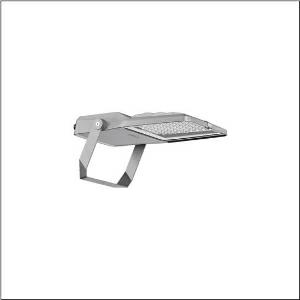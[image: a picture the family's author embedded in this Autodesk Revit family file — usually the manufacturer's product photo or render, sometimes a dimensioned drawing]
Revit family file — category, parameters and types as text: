
# Revit family: floodlight_fl_21_iq_mini___pl52_5xa7772c3d1a_c98d
name_source: partatom
category: Lighting Fixtures
units: mm (PartAtom-declared; Revit-internal decimal feet)

## family parameters
Cut with Voids When Loaded = No
Host = Face
Light Source = No
Part Type = Normal
Room Calculation Point = No
Round Connector Dimension = Use Diameter
Shared = No

## types (1)
- --- (1 x LED, 10510 lm, 87.2 W, 3000K)
    Apparent Load = 87 VA
    CIE Flux Codes = 26 60 98 100 100
    Color Rendering = 80
    Color Temperature = 3000K
    Default Elevation = 1800 mm
    Description = Floodlight FL 21 iQ mini, floodlight, primary light control with lens, of PMMA, primary optical cover: protective disc, of toughened safety glass, transparent, light distribution: PL52, light emission: direct distribution, installation type: surface-mounted, LED, High Power LED, rated luminous flux: 10.510lm, luminous efficacy: 121lm/W, light colour: 830, colour temperature: 3000K, control gear: iQ Street-Remote/DALI, control: Street-Remote, Auto-Match, Temp-Guard, Night-Set, Smart-Wire, Desk-Remote (wireless, voltage-free reading and setting of iQ features in the workshop via application-optimized NFC function/RFID function), optimised constant luminous flux control (CLO 2.0), with terminal, 6-pole, mains connection: 220..240V, AC, 50/60Hz, start of lifetime: 87W, end of service life: 92W, reduction: 40W, luminaire housing, of diecast aluminium, powder-coated, Siteco® metallic grey (DB 702S), corrosivity category C5 mid according to DIN EN ISO 12944, suitable for swimming pools, chlorine-resistant, sealing non-destructively replaceable, mounting bracket, of steel, galvanised, powder-coated, Siteco® metallic grey (DB 702S), protection rating (complete): IP66, insulation class (complete): insulation class II (safety insulation), certification: CE, ENEC, VDE, protection symbol: D, impact resistance: IK08, permissible operating ambient temperature: -40..+40°C, permissible operating ambient temperature for outdoor applications: -40..+50°C, standard: DIN EN 12944, LABS conformity tested according to VDMA 24364:2018-05, packaging unit: 1 piece

Light Distribution: PL52
    Height = 70 mm
    Lamp = 1 x LED
    Lamp Light Flux = 10510 lm
    Lamp Power = 87.2 W
    Lamp count = 1
    Length = 485 mm
    Luminous efficacy = 121 lm/W
    Manufacturer = Siteco
    ModVariant = No
    Model = 5XA7772C3D1A
    Number of Poles = 1
    OnlyDefault = Yes
    Power Factor = 1
    Product Name = Floodlight FL 21 iQ mini | PL52
    Product group = floodlight | pylon annexe
    ProductGroupID = 6200
    Protection Class = Protection class II
    Protection Degree = IP 66
    RLX_Detail_Level = 1
    RLX_Emergency_Light_Flux = 0 lm
    RLX_Emergency_Type = 0
    RLX_Emergency_Type_DB = No
    RlxData = <blob elided: 96577 chars, md5=02f90ad6>
    Socket = socket
    Standby Power = 0 W
    System Light Flux = 10510 lm
    System Power = 87 W
    Type Comments = factory setting: luminous flux: 100 % | dim-lin: 254 | 456 mA
    Type Image = l_1006845.jpg
    URL = http://relux.com
    VarID = @adj_164268
    Voltage = 0 V
    Weight = 0.00 kg
    Width = 337 mm

## geometry (parser evidence)
native form markers: Blend x4, Sweep x11
no freeform markers — native parametric forms only
